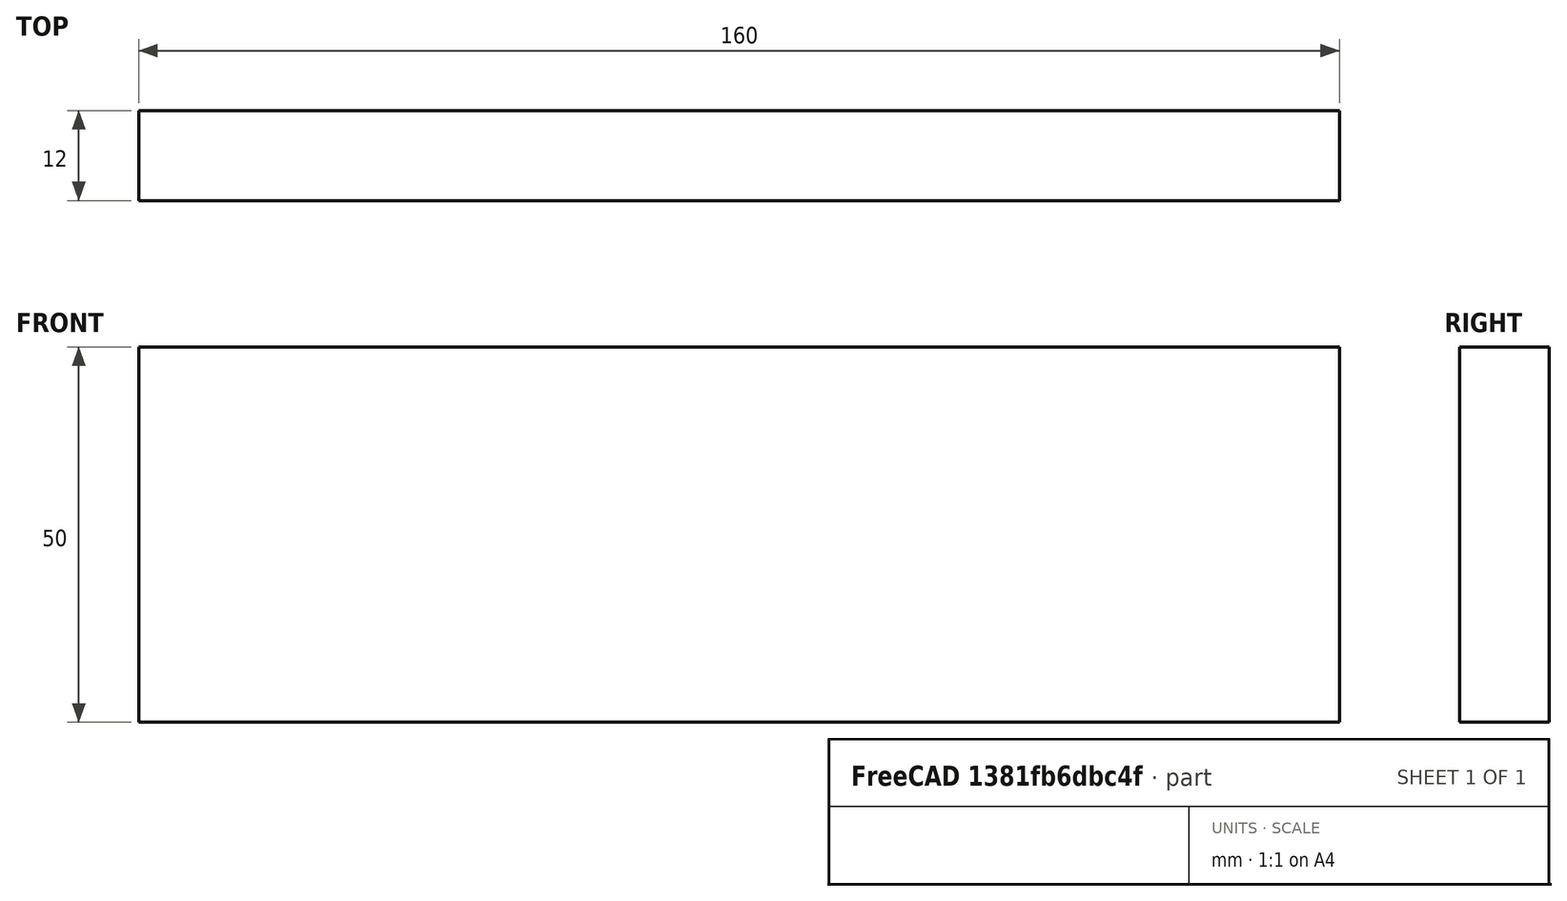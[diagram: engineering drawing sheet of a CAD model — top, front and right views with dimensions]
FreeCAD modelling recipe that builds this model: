
FCSTD DOCUMENT  (FreeCAD 0.15R4671 (Git))
Label: Flat Bar 160x12 EN10058 S235JR
License: All rights reserved
LicenseURL: http://en.wikipedia.org/wiki/All_rights_reserved
objects: Sketcher::SketchObject×1, Part::Extrusion×1
note: 2 computed .brp shape members not serialized (recipe doc carries the construction recipe); baked Part::Feature solids carry a one-line shape summary decoded from their .brp

FEATURE [Sketcher::SketchObject] Sketch
  sketch-geometry (4):
    g0: LineSegment StartX=-80 StartY=-6 StartZ=0 EndX=80 EndY=-6 EndZ=0
    g1: LineSegment StartX=80 StartY=-6 StartZ=0 EndX=80 EndY=6 EndZ=0
    g2: LineSegment StartX=80 StartY=6 StartZ=0 EndX=-80 EndY=6 EndZ=0
    g3: LineSegment StartX=-80 StartY=6 StartZ=0 EndX=-80 EndY=-6 EndZ=0
  constraints (12):
    c: Coincident(g0,g1)
    c: Coincident(g1,g2)
    c: Coincident(g2,g3)
    c: Coincident(g3,g0)
    c: Horizontal(g0)
    c: Horizontal(g2)
    c: Vertical(g1)
    c: Vertical(g3)
    c: Symmetric(g1,g2,g-2)
    c: Symmetric(g0,g1,g-1)
    c: DistanceY(g1) = 12
    c: DistanceX(g0) = 160
FEATURE [Part::Extrusion] Extrude  label="Flat Bar 160x12 EN10058 S235JR"
  Base = -> Sketch
  Dir = (0,0,50)
  Solid = true
